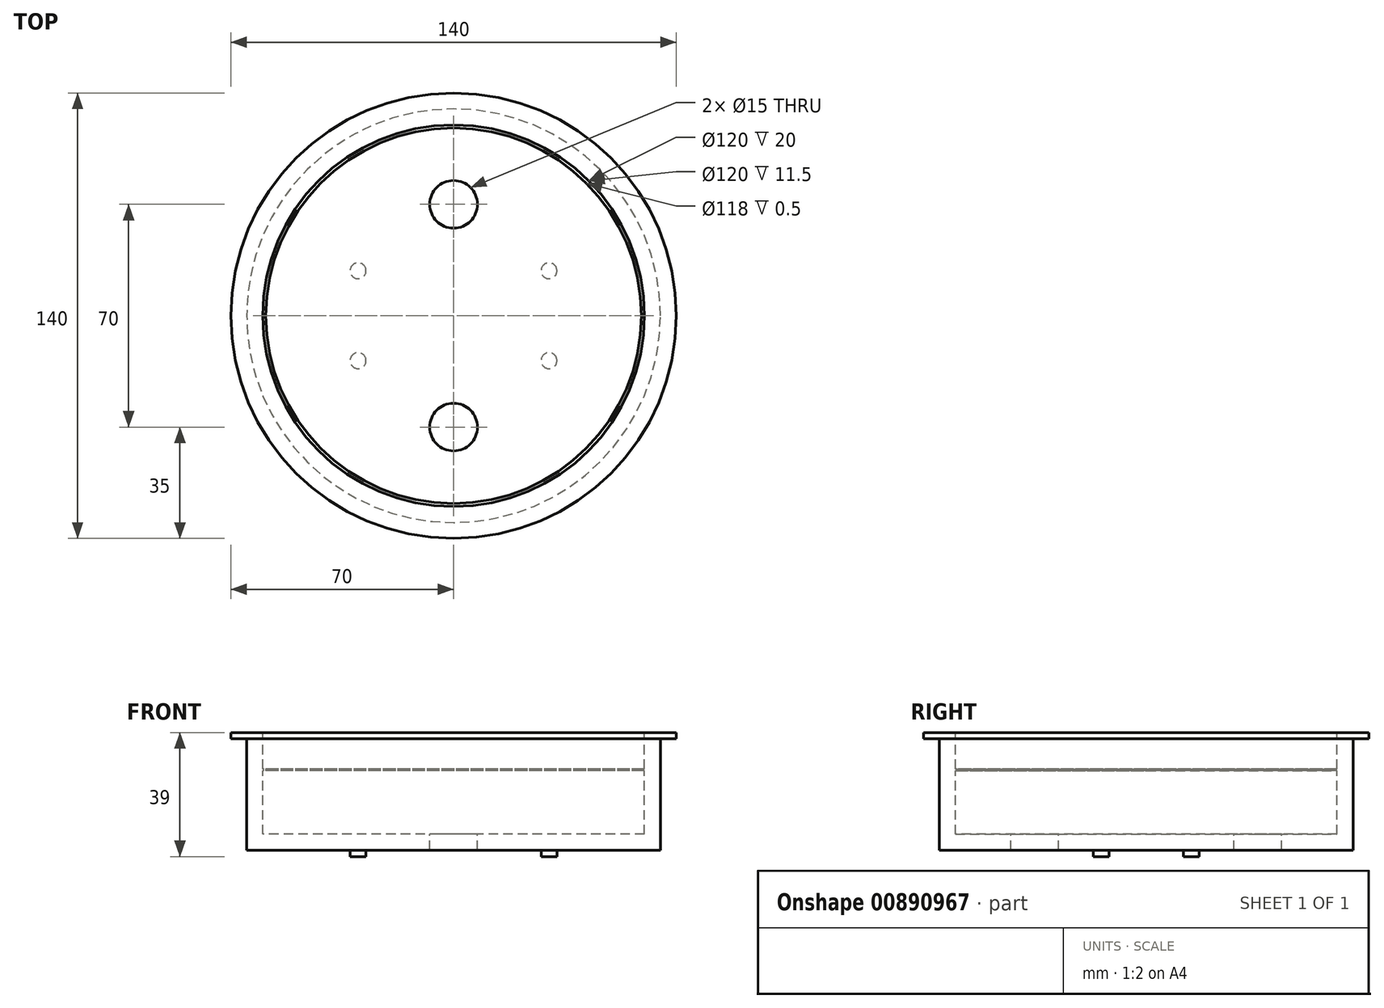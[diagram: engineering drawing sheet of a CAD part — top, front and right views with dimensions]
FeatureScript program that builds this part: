
annotation { "Feature Type Name" : "Feature", "Feature Type Description" : "" }
export const myFeature = defineFeature(function(context is Context, id is Id, definition is map)
    precondition{}
    {
        {
            var Q0;
            Q0=qCreatedBy(makeId("Top.planeOp"),FACE);
            var sketch = newSketch(context, id + "F0", { "sketchPlane" : qUnion([Q0])});
            skCircle(sketch, "E0", {"center": v(0, 0) * mm, "radius": 70 * mm});
            skSolve(sketch);
        }
        {
            var Q0;
            Q0 = qSketchRegion(id + "F0", true);
            extrude(context, id + "F1", {"entities" : qUnion([Q0]), "oppositeDirection" : true, "depth" : 2 * mm, "offsetDistance" : 25 * mm});
        }
        {
            var Q0;
            Q0=makeQuery(id+"F1.opExtrude","CAP_FACE",FACE,{"disambiguationData":[OSD([sQuery(id+"F0.wireOp",EDGE,"E0")])],"isStart":false});
            var sketch = newSketch(context, id + "F2", { "sketchPlane" : qUnion([Q0])});
            skCircle(sketch, "E1", {"center": v(0, 0) * mm, "radius": 65 * mm});
            skSolve(sketch);
        }
        {
            var Q0;
            Q0 = qSketchRegion(id + "F2", true);
            extrude(context, id + "F3", {"entities" : qUnion([Q0]), "operationType" : NewBodyOperationType.ADD, "depth" : 35 * mm, "offsetDistance" : 25 * mm});
        }
        {
            var Q0;
            Q0=makeQuery(id+"F1.opExtrude","CAP_FACE",FACE,{"disambiguationData":[OSD([sQuery(id+"F0.wireOp",EDGE,"E0")])],"isStart":true});
            var sketch = newSketch(context, id + "F4", { "sketchPlane" : qUnion([Q0])});
            skCircle(sketch, "E2", {"center": v(0, 0) * mm, "radius": 60 * mm});
            skSolve(sketch);
        }
        {
            var Q0;
            Q0 = qSketchRegion(id + "F4", true);
            extrude(context, id + "F5", {"entities" : qUnion([Q0]), "operationType" : NewBodyOperationType.REMOVE, "oppositeDirection" : true, "depth" : 32 * mm, "offsetDistance" : 25 * mm});
        }
        {
            var Q0;
            Q0=makeQuery(id+"F5.boolean.opBoolean","COPY",FACE,{"derivedFrom":makeQuery(id+"F5.opExtrude","CAP_FACE",FACE,{"disambiguationData":[OSD([sQuery(id+"F4.wireOp",EDGE,"E2")])],"isStart":false})});
            var sketch = newSketch(context, id + "F6", { "sketchPlane" : qUnion([Q0])});
            skCircle(sketch, "E3", {"center": v(0, -35) * mm, "radius": 7.5 * mm});
            skCircle(sketch, "E4.MirrorC", {"center": v(0, 35) * mm, "radius": 7.5 * mm});
            skSolve(sketch);
        }
        {
            var Q0;
            Q0 = qSketchRegion(id + "F6", true);
            extrude(context, id + "F7", {"entities" : qUnion([Q0]), "operationType" : NewBodyOperationType.REMOVE, "endBound" : BoundingType.THROUGH_ALL, "oppositeDirection" : true, "depth" : 25 * mm, "offsetDistance" : 25 * mm});
        }
        {
            var Q0;
            Q0=makeQuery(id+"F3.opExtrude","CAP_FACE",FACE,{"disambiguationData":[OSD([sQuery(id+"F2.wireOp",EDGE,"E1")])],"isStart":false});
            var sketch = newSketch(context, id + "F8", { "sketchPlane" : qUnion([Q0])});
            skCircle(sketch, "E5", {"center": v(-30, 14.13) * mm, "radius": 2.5 * mm});
            skCircle(sketch, "E6", {"center": v(-30, -14.13) * mm, "radius": 2.5 * mm});
            skCircle(sketch, "E7.MirrorC", {"center": v(30, 14.13) * mm, "radius": 2.5 * mm});
            skCircle(sketch, "E8.MirrorC", {"center": v(30, -14.13) * mm, "radius": 2.5 * mm});
            skSolve(sketch);
        }
        {
            var Q0;
            Q0 = qSketchRegion(id + "F8", true);
            extrude(context, id + "F9", {"entities" : qUnion([Q0]), "operationType" : NewBodyOperationType.ADD, "depth" : 2 * mm, "offsetDistance" : 25 * mm});
        }
        {
            var Q0;
            Q0=makeQuery(id+"F5.boolean.opBoolean","COPY",FACE,{"derivedFrom":makeQuery(id+"F5.opExtrude","CAP_FACE",FACE,{"disambiguationData":[OSD([sQuery(id+"F4.wireOp",EDGE,"E2")])],"isStart":false})});
            cPlane(context, id + "F10", {"entities" : qUnion([Q0]), "cplaneType" : CPlaneType.OFFSET, "offset" : 20 * mm, "width" : 150 * mm, "height" : 150 * mm});
        }
        {
            var Q0;
            Q0=qCreatedBy(id+"F10.planeOp",FACE);
            var sketch = newSketch(context, id + "F11", { "sketchPlane" : qUnion([Q0])});
            skCircle(sketch, "E9", {"center": v(0, 0) * mm, "radius": 62.2 * mm});
            skCircle(sketch, "E10", {"center": v(0, 0) * mm, "radius": 59 * mm});
            skSolve(sketch);
        }
        {
            var Q0;
            Q0 = qSketchRegion(id + "F11", true);
            extrude(context, id + "F12", {"entities" : qUnion([Q0]), "operationType" : NewBodyOperationType.ADD, "depth" : 0.5 * mm, "offsetDistance" : 25 * mm});
        }
    });
